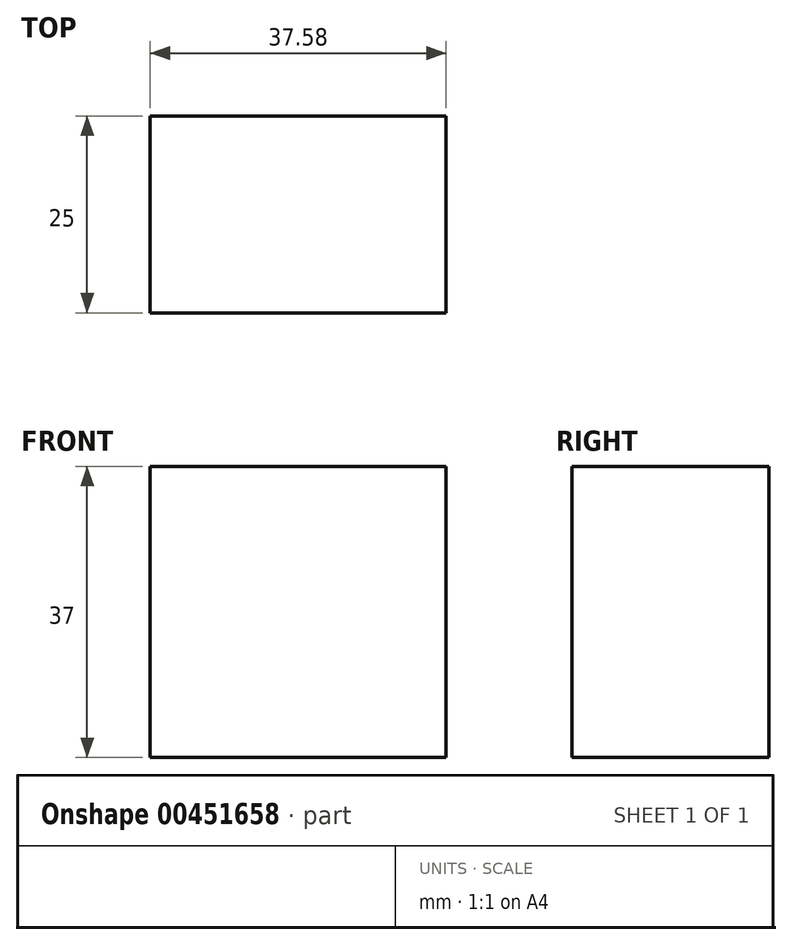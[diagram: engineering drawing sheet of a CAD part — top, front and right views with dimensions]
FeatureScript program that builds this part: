
annotation { "Feature Type Name" : "Feature", "Feature Type Description" : "" }
export const myFeature = defineFeature(function(context is Context, id is Id, definition is map)
    precondition{}
    {
        {
            var Q0;
            Q0=qCreatedBy(makeId("Front.planeOp"),FACE);
            var sketch = newSketch(context, id + "F0", { "sketchPlane" : qUnion([Q0])});
            skLineSegment(sketch, "E0.bottom", {"start": v(-57.81, 3.76) * mm, "end": v(-20.23, 3.76) * mm});
            skLineSegment(sketch, "E0.top", {"start": v(-57.81, 40.76) * mm, "end": v(-20.23, 40.76) * mm});
            skLineSegment(sketch, "E0.left", {"start": v(-57.81, 3.76) * mm, "end": v(-57.81, 40.76) * mm});
            skLineSegment(sketch, "E0.right", {"start": v(-20.23, 3.76) * mm, "end": v(-20.23, 40.76) * mm});
            skPoint(sketch, "E0.middle", {"position": v(-39.02, 22.26) * mm});
            skSolve(sketch);
        }
        {
            var Q0;
            Q0=makeQuery(id+"F0.imprint","IMPRINT",FACE,{"disambiguationData":[TD([[makeQuery(id+"F0.imprint","IMPRINT",EDGE,{"derivedFrom":sQuery(id+"F0.wireOp",EDGE,"E0.bottom")}),1.0]])]});
            extrude(context, id + "F1", {"entities" : qUnion([Q0]), "depth" : 25 * mm});
        }
    });
